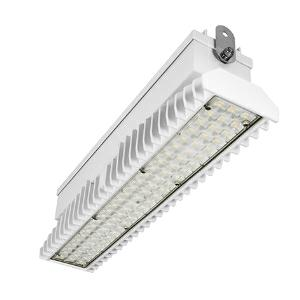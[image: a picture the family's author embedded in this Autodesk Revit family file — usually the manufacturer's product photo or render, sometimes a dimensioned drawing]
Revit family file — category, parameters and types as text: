
# Revit family: 3f_filippi_-_3f_lem_ampio_3f_filippi_-_58899_a0811_-_3f_lem_1_led_50_dali_cr_ampio___vt_c1a0
name_source: partatom
category: Lighting Fixtures
units: mm (PartAtom-declared; Revit-internal decimal feet)

## family parameters
Cut with Voids When Loaded = No
Host = Face
Light Source = No
Part Type = Normal
Room Calculation Point = No
Round Connector Dimension = Use Diameter
Shared = No

## types (1)
- 3F Filippi - 3F LEM Ampio (1 x LED, 7910 lm, 56 W, 4000 K)
    Apparent Load = 56 VA
    Approval mark = CE
    CIE Flux Codes = 60 92 99 100 100
    Color Rendering = 80
    Color Temperature = 4000 K
    Control Gear = Electronic transformer
    Default Elevation = 1800 mm
    Description = Industrial luminaire with high light output and high luminous efficiency designed with the most innovative technologies for environments with temperature up to 55°C.

ILLUMINOTECHNICAL
Luminous efficiency 100% (DLOR 99%, ULOR 1%).
Initial luminous flux of the luminaire 7910 lm.
Direct symmetric wide distribution: the illuminated area has a rectangular shape.
Installation Interdistance Transv.D = 1.58 x hu - Long.D = 1.45 x hu.
Tabular UGR (CIE 117 - 4H-8H; S=0.25H; 70/50/20): RUG 26 - 26.8.
Beam angle: 93° - 99°.
Luminous efficacy 141 lm/W.
Lifetime (L93/B10): 30000 h. (tq+25°C)
Lifetime (L90/B10): 50000 h. (tq+25°C)
Lifetime (L85/B10): 80000 h. (tq+25°C)
Lifetime (L80/B10): 100000 h. (tq+25°C)
Lifetime (L85/B10): 50000 h. (tq+55°C)
Sudden decreased luminous flux after 50000 hours: 0% (C0).
Photobiological safety in compliance with IEC/TR 62778: RG0 risk exempt, (IEC 62471).
In compliance with IEC/EN 62722-2-1 - IEC/EN 62717 standards.

SOURCE
Mid-Power linear LED module 50W/840.
Energy efficiency class (UE 2019/2020 - UE 2019/2015): C.
CIE 13.3 Colour rendering index: CRI >80 (R9 <50%).
IES TM-30 Fidelity Index: Rf = 84 Rg = 95.
CCT nominal colour temperature 4000 K.
Colour initial tolerance (MacAdam): SDCM 3.

MECHANICAL
Passive modular heatsinks in die-casted aluminium, painted in white colour.
To optimize the thermal management of the LED module, the heatsinks are oversized and provided with self-cleaning of cooling fins.
Wiring body in aluminium and galvanised steel anchored solidly to the sinks and thermally separated.
3F Lens lenses with high luminous efficiency, transparent methacrylate (PMMA), fixed to the LED modules.
Fixing brackets in stainless steel.
Luminaire with limited surface temperature. - D - (EN 60598-2-24)
Dimensions: 542x115 mm, height 154 mm. Weight 6.772 kg.
IP65 protection degree.
Mechanical strength to impacts IK06 (1 joule).
Glow-wire test resistance 650°C.

ELECTRICAL
Halogen Free DALI-2 DATI (Parts 251, 252, 253), PUSH-DIM, electronic wiring 230V-50/60Hz, power factor 0.95 at full load, THD <25%, constant output current, class I, 1 driver, 1 DALI addresse.
Power of the luminaire 56 W.
ENEC - CE.
SAFE FLICKER: PstLM=<1 and SVM=<0.4 (IEC TR 61547-1 and IEC TR 63158), to ensure a more comfortable and safe light.
Luminaire compliant with EN 60598-2-22 for power supply from a centralised emergency system CPSS (Central Power Supply System), not incorporated in the luminaire - high risk areas excluded. The default power and flux are 100% in AC and 15% in DC.
Ambient temperature from -30°C to +55°C.
Temperature class T6 max 85°C.
Quick connection via M25 5P connector with 9-13 mm tightening range.
Power unit positioned on a separate compartment by the LED module to ensure optimum temperatures of cabling components, to be inspectable and maintainable.
Relative humidity UR: <85%.

INSTALLATION
Ceiling / Suspended / Wall.
All accessories dedicated to this product are available on the Catalog and on our website www.3F-Filippi.com.

ACCESSORIES
A0811 - VT transparent glass, tempered, not flammable, with sealing gasket.
One required for each light module. The pack contains 10 pieces.

APPLICATIONS
In commercial environments, exhibition and industrial areas, stores, open areas.
Applications with high ambient temperature up to 55°C.
Environments in which it is necessary a total protection against falling fragments (eg environments with foodstuffs or machines with moving parts or with extreme temperature changes), use luminaires with polycarbonate lenses.

LIGHT MANAGEMENT
Recommended minimum setting: 10%.
The luminaire, equipped with (DALI-2 DATI) driver, can be controlled manually with 3F Easy Dim technology or automatically/manually with wired or wireless DALI/D2D control systems.
The D2D driver guarantees interoperability with other devices with the same certification by making the following information available:
Device Data (Part 251), Energy Report (Part 252), Diagnosis & Maintenance (Part 253).
In electrical systems without a regulation system (manual or automatic) and DALI bus, a suitable jumper must be made on the DA-DA terminals of the appliance.

WARNING
Fixture not suitable for cold stores with an ambient temperature <0°C and/or relative humidity >85%.
Luminaire designed for disposal/recycling at end-of-life.
Replaceable (LED only) light source by a professional. Replaceable control gear by a professional.
    Height = 154 mm
    Lamp = 1 x LED
    Lamp Light Flux = 7910 lm
    Lamp Power = 56 W
    Lamp count = 1
    Length = 542 mm
    Lifetime = 50000 h
    Luminous efficacy = 141 lm/W
    Manufacturer = 3F Filippi
    ModVariant = No
    Model = 3F Filippi - 58899+A0811 - 3F LEM 1 LED 50 DALI CR AMPIO + VT
    Mounting Place = Ceiling
    Mounting Type = Pendant
    Number of Poles = 1
    OnlyDefault = Yes
    Power Factor = 1
    Product Name = 3F Filippi - 3F LEM Ampio
    Product group = pendant luminaire
    ProductGroupID = 9
    Protection Class = Protection class I
    Protection Degree = IP 65
    RLX_Detail_Level = 1
    RLX_Emergency_Light_Flux = 0 lm
    RLX_Emergency_Type = 0
    RLX_Emergency_Type_DB = No
    RlxData = <blob elided: 96853 chars, md5=e6d1e297>
    Socket = socket
    Standby Power = 0 W
    System Light Flux = 7910 lm
    System Power = 56 W
    Type Comments = Product without accessories
    Type Image = 3f_filippi_-_lem_1__a0811.jpg
    URL = http://relux.com
    VarID = ---
    Voltage = 0 V
    Weight = 0.00 kg
    Width = 115 mm

## geometry (parser evidence)
native form markers: Blend x4, Sweep x12
no freeform markers — native parametric forms only
